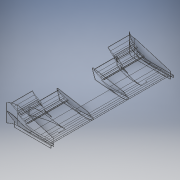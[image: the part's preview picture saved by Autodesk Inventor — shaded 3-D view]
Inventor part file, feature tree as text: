
AUTODESK INVENTOR PART (.ipt)
format: ipt  version: 2018 (Build 220112000, 112)  size: 922,112 bytes
history: native  units: mm
features: extrude x16, sketch x16, projected_geometry x12, other x4, chamfer x1, mirror x1
ambient origin geometry x8: Origin, YZ Plane, XZ Plane, XY Plane, X Axis, Y Axis, Z Axis, Center Point
bodies: Body1 (feature_tree)
feature tree (50):
  extrude  "押し出し7"  Depth=394.0mm TaperAngle=0.0deg
  extrude  "押し出し8"  Depth=5.0mm TaperAngle=0.0deg
  extrude  "押し出し9"  Depth=225.0mm TaperAngle=0.0deg
  extrude  "押し出し10"  Depth=5.0mm TaperAngle=0.0deg
  extrude  "押し出し11"  Depth=225.0mm TaperAngle=0.0deg
  extrude  "押し出し13"  Depth=2.0mm
  other  "厚み1"
  other  "厚み2"
  chamfer  "面取り1"  Distance=5.0mm
  extrude  "押し出し16"  Depth=225.0mm TaperAngle=0.0deg
  extrude  "押し出し17"  Depth=1.0mm
  extrude  "押し出し18"  Depth=1.0mm
  extrude  "押し出し20"  Depth=2.0mm
  extrude  "押し出し21"  Depth=2.0mm TaperAngle=45.0deg
  extrude  "押し出し22"  Depth=10.0mm TaperAngle=0.0deg
  extrude  "押し出し23"  Depth=5.0mm
  other  "面を削除1"
  extrude  "押し出し24"  Depth=2.0mm
  extrude  "押し出し25"  TaperAngle=0.0deg  [1 undecoded]
  extrude  "押し出し27"  Depth=35.0mm TaperAngle=0.0deg
  mirror  "ミラー6"
  other  "ソリッド36"
  sketch  "スケッチ8"
  projected_geometry  "投影ループ7"
  sketch  "スケッチ9"
  projected_geometry  "投影ループ8"
  sketch  "スケッチ10"
  projected_geometry  "投影ループ9"
  projected_geometry  "投影ループ10"
  sketch  "スケッチ11"
  projected_geometry  "投影ループ11"
  sketch  "スケッチ12"
  projected_geometry  "投影ループ12"
  projected_geometry  "投影ループ13"
  projected_geometry  "投影ループ14"
  sketch  "スケッチ14"
  projected_geometry  "投影ループ16"
  sketch  "スケッチ18"
  sketch  "スケッチ19"
  sketch  "スケッチ20"
  sketch  "スケッチ21"
  sketch  "スケッチ22"
  sketch  "スケッチ23"
  projected_geometry  "投影ループ18"
  sketch  "スケッチ24"
  projected_geometry  "投影ループ19"
  sketch  "スケッチ25"
  projected_geometry  "投影ループ20"
  sketch  "スケッチ26"
  sketch  "スケッチ27"
note: 1 required parameter value undecoded (feature->parameter linkage not recoverable at this tier; creation-order binding heuristic only, values carry confidence <= 0.55)
